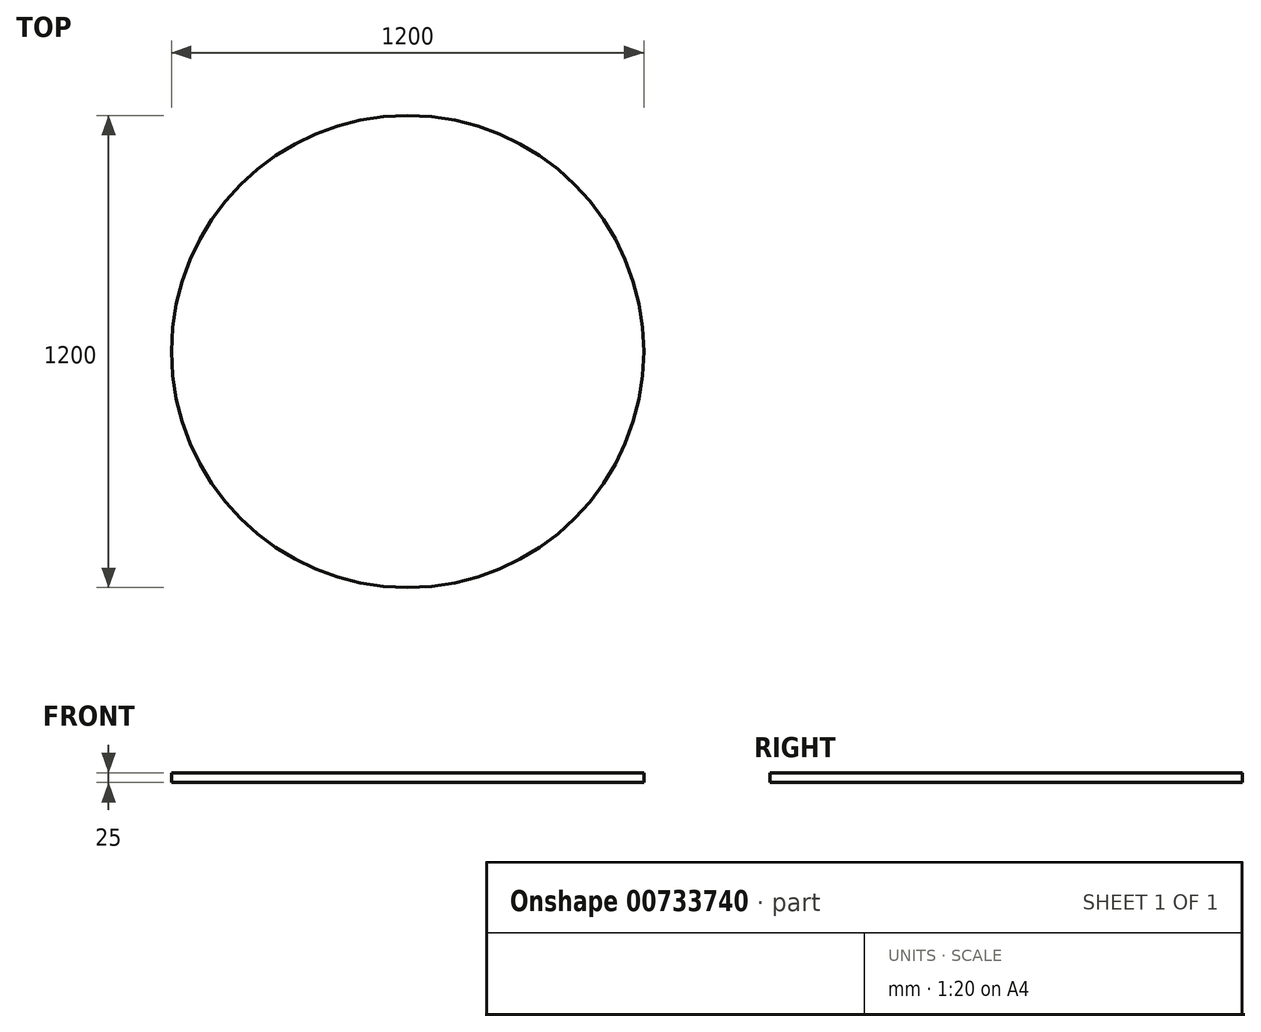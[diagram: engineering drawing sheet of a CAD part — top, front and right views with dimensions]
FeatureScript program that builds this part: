
annotation { "Feature Type Name" : "Feature", "Feature Type Description" : "" }
export const myFeature = defineFeature(function(context is Context, id is Id, definition is map)
    precondition{}
    {
        {
            var Q0;
            Q0=qCreatedBy(makeId("Top.planeOp"),FACE);
            var sketch = newSketch(context, id + "F0", { "sketchPlane" : qUnion([Q0])});
            skCircle(sketch, "E0", {"center": v(0, 0) * mm, "radius": 600 * mm});
            skSolve(sketch);
        }
        {
            var Q0;
            Q0=makeQuery(id+"F0.imprint","IMPRINT",FACE,{"disambiguationData":[TD([[makeQuery(id+"F0.imprint","IMPRINT",EDGE,{"derivedFrom":sQuery(id+"F0.wireOp",EDGE,"E0")}),1.0]])]});
            extrude(context, id + "F1", {"entities" : qUnion([Q0]), "depth" : 25 * mm, "offsetDistance" : 25 * mm});
        }
    });
